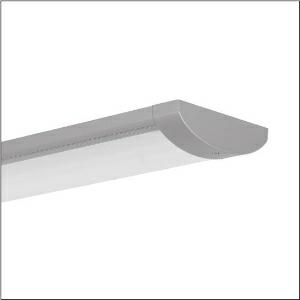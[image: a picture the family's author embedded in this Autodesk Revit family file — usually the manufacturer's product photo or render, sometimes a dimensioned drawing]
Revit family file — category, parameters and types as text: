
# Revit family: tv_20_5xa86174n0j
name_source: partatom
category: Lighting Fixtures
units: mm (PartAtom-declared; Revit-internal decimal feet)

## family parameters
Cut with Voids When Loaded = No
Host = Face
Light Source = No
Part Type = Normal
Room Calculation Point = No
Round Connector Dimension = Use Diameter
Shared = No

## types (1)
- TV 20 (1 x LED 4000K / CRI = 80 (unbekannt), 3960 lm, 4000K)
    Apparent Load = 37 VA
    CIE Flux Codes = 48 78 95 99 100
    Color Rendering = 80
    Color Temperature = 4000K
    Default Elevation = 1800 mm
    Description = TV 20, vandal-proof luminaire, primary light control with specular reflector, of aluminium, matt, primary optical cover: enclosure, of PC, frosted, light emission: direct distribution, primary light characteristic: symmetric, installation type: surface-mounted, LED rated luminous flux: 3.960 lm, light colour: 840, colour temperature: 4000K, control gear: ECG, mains connection: 230V, AC, 50Hz, rated input power: 37W, luminaire housing, of aluminium, coated, Siteco® metallic grey (DB 702S), length: 1.261 mm, width: 260 mm, height: 70mm, protection rating (complete): IP65, insulation class (complete): insulation class I (protective earthing), certification: CE, protection symbol: F, impact resistance: 2x IK10, standard: EN 60598, packaging unit: 1 piece
    Height = 70 mm
    Lamp = 1 x LED 4000K / CRI >= 80 (unbekannt)
    Lamp Light Flux = 3960 lm
    Lamp count = 1
    Length = 1261 mm
    Luminous efficacy = 107 lm/W
    Manufacturer = Siteco
    ModVariant = No
    Model = 5XA86174N0J
    Mounting Place = Ceiling
    Mounting Type = Surface mounted
    Number of Poles = 1
    OnlyDefault = Yes
    Power Factor = 1
    Product Name = TV 20
    Product group = vandal-proof luminaire
    ProductGroupID = 307
    Protection Class = Protection class I
    Protection Degree = IP 65
    RLX_Detail_Level = 1
    RlxData = <blob elided: 25597 chars, md5=6b21a52a>
    Socket = socket
    Standby Power = 0 W
    System Light Flux = 3960 lm
    System Power = 37 W
    Type Comments = Product without accessories
    Type Image = l_1004809.jpg
    URL = http://relux.com
    VarID = ---
    Voltage = 0 V
    Weight = 0.00 kg
    Width = 260 mm

## geometry (parser evidence)
native form markers: Blend x4, Sweep x10
no freeform markers — native parametric forms only
